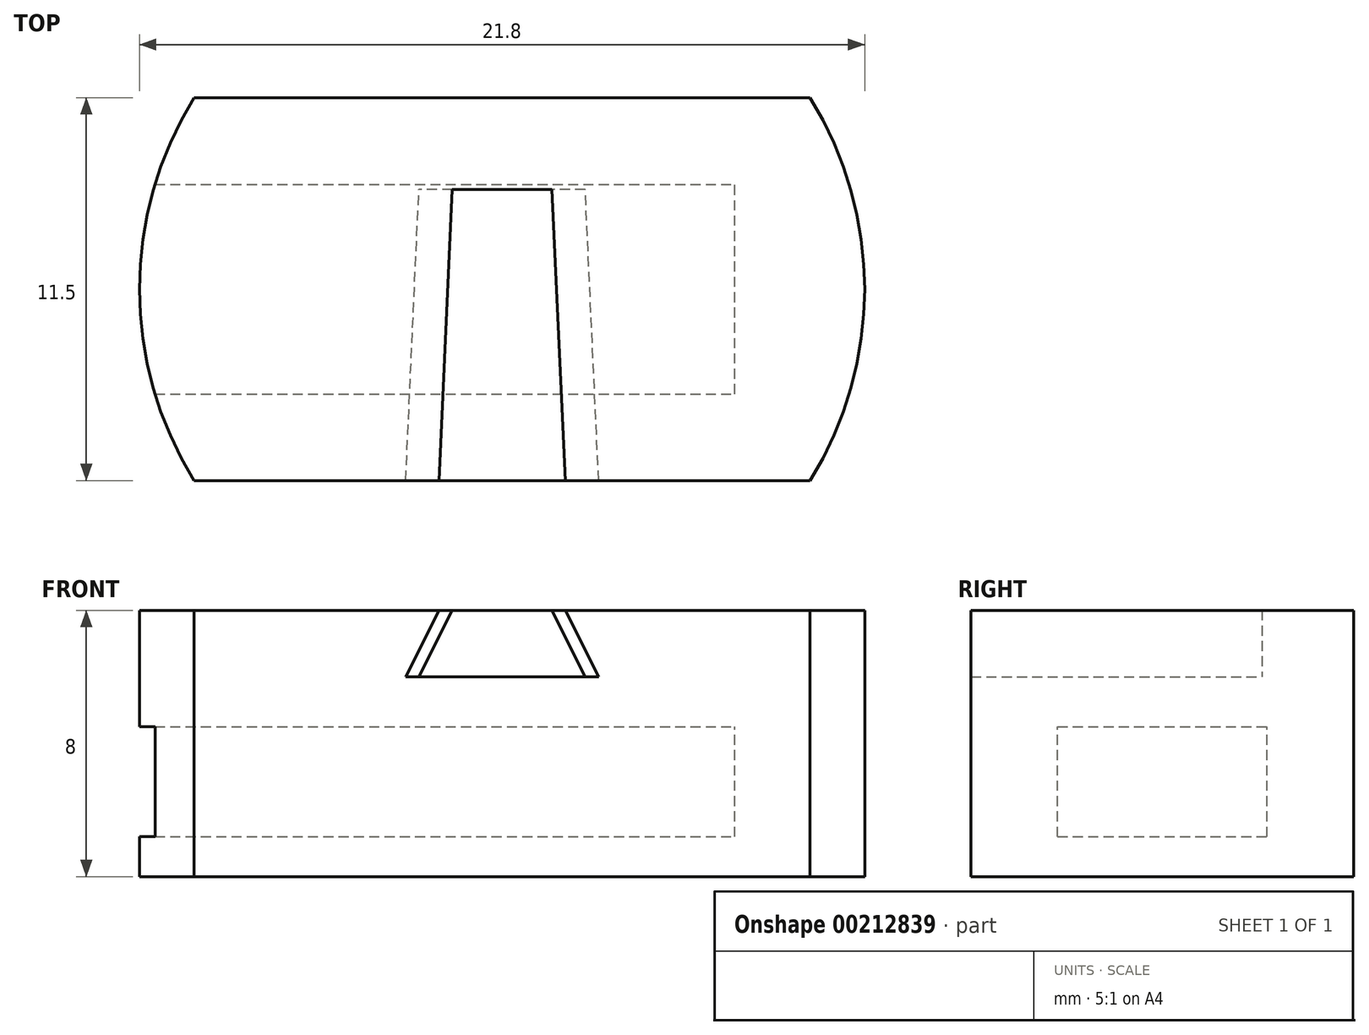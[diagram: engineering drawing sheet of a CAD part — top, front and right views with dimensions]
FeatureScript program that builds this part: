
annotation { "Feature Type Name" : "Feature", "Feature Type Description" : "" }
export const myFeature = defineFeature(function(context is Context, id is Id, definition is map)
    precondition{}
    {
        {
            var Q0;
            Q0=qCreatedBy(makeId("Top.planeOp"),FACE);
            var sketch = newSketch(context, id + "F0", { "sketchPlane" : qUnion([Q0])});
            skLineSegment(sketch, "E0.bottom", {"start": v(8.79, 5.75) * mm, "end": v(-8.79, 5.75) * mm});
            skLineSegment(sketch, "E0.top", {"start": v(8.79, -5.75) * mm, "end": v(-8.79, -5.75) * mm});
            skPoint(sketch, "E0.middle", {"position": v(0, 0) * mm});
            skArc(sketch, "E1", {"start": v(-8.79, 5.75) * mm, "mid": v(-10.5, 0) * mm, "end": v(-8.79, -5.75) * mm, "construction": true});
            skArc(sketch, "E2.trimOffspring", {"start": v(8.79, -5.75) * mm, "mid": v(10.5, 0) * mm, "end": v(8.79, 5.75) * mm, "construction": true});
            skArc(sketch, "E3.0", {"start": v(-9.26, 5.75) * mm, "mid": v(-10.9, 0) * mm, "end": v(-9.26, -5.75) * mm});
            skLineSegment(sketch, "E4", {"start": v(-8.79, -5.75) * mm, "end": v(-9.26, -5.75) * mm});
            skLineSegment(sketch, "E5", {"start": v(-8.79, 5.75) * mm, "end": v(-9.26, 5.75) * mm});
            skArc(sketch, "E6.MirrorCS", {"start": v(9.26, 5.75) * mm, "mid": v(10.9, 0) * mm, "end": v(9.26, -5.75) * mm});
            skLineSegment(sketch, "E7", {"start": v(8.79, 5.75) * mm, "end": v(9.26, 5.75) * mm});
            skLineSegment(sketch, "E8", {"start": v(8.79, -5.75) * mm, "end": v(9.26, -5.75) * mm});
            skSolve(sketch);
        }
        {
            var Q0;
            Q0=makeQuery(id+"F0.imprint","IMPRINT",FACE,{"disambiguationData":[TD([[makeQuery(id+"F0.imprint","IMPRINT",EDGE,{"derivedFrom":sQuery(id+"F0.wireOp",EDGE,"E0.bottom")}),1.0]])]});
            extrude(context, id + "F1", {"entities" : qUnion([Q0]), "oppositeDirection" : true, "depth" : 8 * mm});
        }
        {
            var Q0;
            Q0=makeQuery(id+"F1.opExtrude","SWEPT_FACE",FACE,{"disambiguationData":[OSD([sQuery(id+"F0.wireOp",EDGE,"E0.top")])]});
            var sketch = newSketch(context, id + "F2", { "sketchPlane" : qUnion([Q0])});
            skLineSegment(sketch, "E9", {"start": v(-1.9, 0) * mm, "end": v(-2.9, -2) * mm});
            skLineSegment(sketch, "E10.MirrorCS", {"start": v(1.9, 0) * mm, "end": v(2.9, -2) * mm});
            skLineSegment(sketch, "E11", {"start": v(1.9, 0) * mm, "end": v(-1.9, 0) * mm});
            skLineSegment(sketch, "E12", {"start": v(2.9, -2) * mm, "end": v(-2.9, -2) * mm});
            skSolve(sketch);
        }
        {
            var Q0;
            Q0=qCreatedBy(makeId("Front.planeOp"),FACE);
            cPlane(context, id + "F3", {"entities" : qUnion([Q0]), "cplaneType" : CPlaneType.OFFSET, "offset" : 3 * mm, "oppositeDirection" : true, "width" : 150 * mm, "height" : 150 * mm});
        }
        {
            var Q0;
            Q0=qCreatedBy(id+"F3.planeOp",FACE);
            var sketch = newSketch(context, id + "F4", { "sketchPlane" : qUnion([Q0])});
            skLineSegment(sketch, "E13.0", {"start": v(1.9, 0) * mm, "end": v(2.9, -2) * mm, "construction": true});
            skLineSegment(sketch, "E13.3", {"start": v(-1.9, 0) * mm, "end": v(-2.9, -2) * mm, "construction": true});
            skLineSegment(sketch, "E14", {"start": v(1.5, 0) * mm, "end": v(2.5, -2) * mm});
            skLineSegment(sketch, "E15.MirrorCS", {"start": v(-1.5, 0) * mm, "end": v(-2.5, -2) * mm});
            skLineSegment(sketch, "E16", {"start": v(1.5, 0) * mm, "end": v(-1.5, 0) * mm});
            skLineSegment(sketch, "E17", {"start": v(2.5, -2) * mm, "end": v(-2.5, -2) * mm});
            skSolve(sketch);
        }
        {
            var Q1;
            Q1 = qSketchRegion(id + "F2", true);
            var Q2;
            Q2 = qSketchRegion(id + "F4", true);
            loft(context, id + "F5", {"operationType" : NewBodyOperationType.REMOVE, "sheetProfilesArray" : [{ "sheetProfileEntities" : qUnion([Q1]) }, { "sheetProfileEntities" : qUnion([Q2]) }]});
        }
        {
            var Q0;
            Q0=qCreatedBy(makeId("Right.planeOp"),FACE);
            var sketch = newSketch(context, id + "F6", { "sketchPlane" : qUnion([Q0])});
            skLineSegment(sketch, "E18.bottom", {"start": v(-3.15, -6.8) * mm, "end": v(3.15, -6.8) * mm});
            skLineSegment(sketch, "E18.top", {"start": v(-3.15, -3.5) * mm, "end": v(3.15, -3.5) * mm});
            skLineSegment(sketch, "E18.left", {"start": v(-3.15, -6.8) * mm, "end": v(-3.15, -3.5) * mm});
            skLineSegment(sketch, "E18.right", {"start": v(3.15, -6.8) * mm, "end": v(3.15, -3.5) * mm});
            skPoint(sketch, "E18.middle", {"position": v(0, -5.15) * mm});
            skSolve(sketch);
        }
        {
            var Q0;
            Q0 = qSketchRegion(id + "F6", true);
            extrude(context, id + "F7", {"entities" : qUnion([Q0]), "operationType" : NewBodyOperationType.REMOVE, "oppositeDirection" : true, "depth" : 11.9 * mm});
        }
        {
            var Q0;
            Q0 = qSketchRegion(id + "F6", true);
            extrude(context, id + "F8", {"entities" : qUnion([Q0]), "operationType" : NewBodyOperationType.REMOVE, "depth" : 7 * mm});
        }
    });
